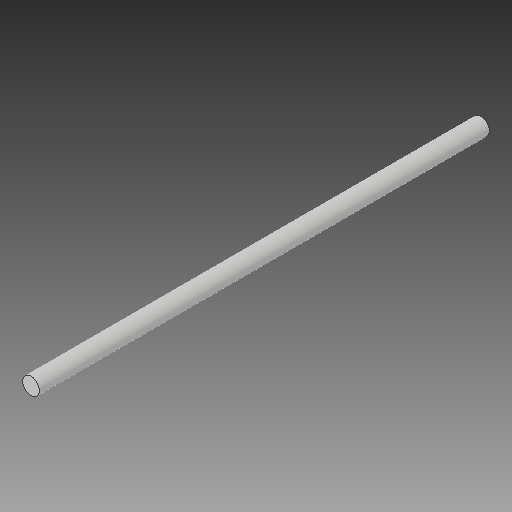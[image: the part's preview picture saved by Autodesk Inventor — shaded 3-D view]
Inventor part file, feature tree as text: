
AUTODESK INVENTOR PART (.ipt)
format: ipt  version: 2017 (Build 210142000, 142)  size: 88,064 bytes
history: native  units: in
note: dims shown in document units (in); Inventor stores cm internally (conversion verified against a paired STEP export)
features: sketch x2, extrude x1
ambient origin geometry x8: Origin, YZ Plane, XZ Plane, XY Plane, X Axis, Y Axis, Z Axis, Center Point
bodies: Solid1 (feature_tree)
feature tree (3):
  sketch  "Sketch1"  dims[d0=0.125in d1=3.3in d2=0.0in]
  extrude  "Extrusion1"  Depth=3.3in TaperAngle=0.0deg
  sketch  "Sketch2"
